# Revit family: WSL_A3-Roof-Light-(1)
name_source: partatom
category: Windows
revit_build: Autodesk Revit 2016 (Build: 20150220_1215(x64)
units: mm (PartAtom-declared; Revit-internal decimal feet)

## family parameters
Always vertical = No
Cut with Voids When Loaded = No
Host = Roof
Room Calculation Point = No
Shared = No

## types (2) — shared parameters
Height = 1980 mm  [stored 6.49606 ft]
Keynote = L10/460
Material Flashing = Metal - Lead
Material Frame = Metal - Bronze,LightBrush
Material Glass = Glass
Material Ironmongery = Metal - Aluminium
Material Sash = Window Frame
Operation = SinglePanel
Rough Height = 1980 mm  [stored 6.49606 ft]
Upstand = 50 mm  [stored 0.164042 ft]
Vert Bar Thickness = 25 mm  [stored 0.082021 ft]
Vis - Ironmongery = Yes
Vis - Vert Bar = Yes

## per-type parameters (varying)
| type | No of Vert Bars | Rough Width | Width |
| 2500mm Long with 4 Bars | 4 | 2500 mm  [stored 8.2021 ft] | 2500 mm  [stored 8.2021 ft] |
| 3500mm Long with 6 Bars | 6 | 3500 mm  [stored 11.4829 ft] | 3500 mm  [stored 11.4829 ft] |

note: [stored X ft] marks values corroborated as IEEE doubles in the binary element streams (Revit-internal decimal feet)

## geometry (parser evidence)
native form markers: Sweep x5
no freeform markers — native parametric forms only
